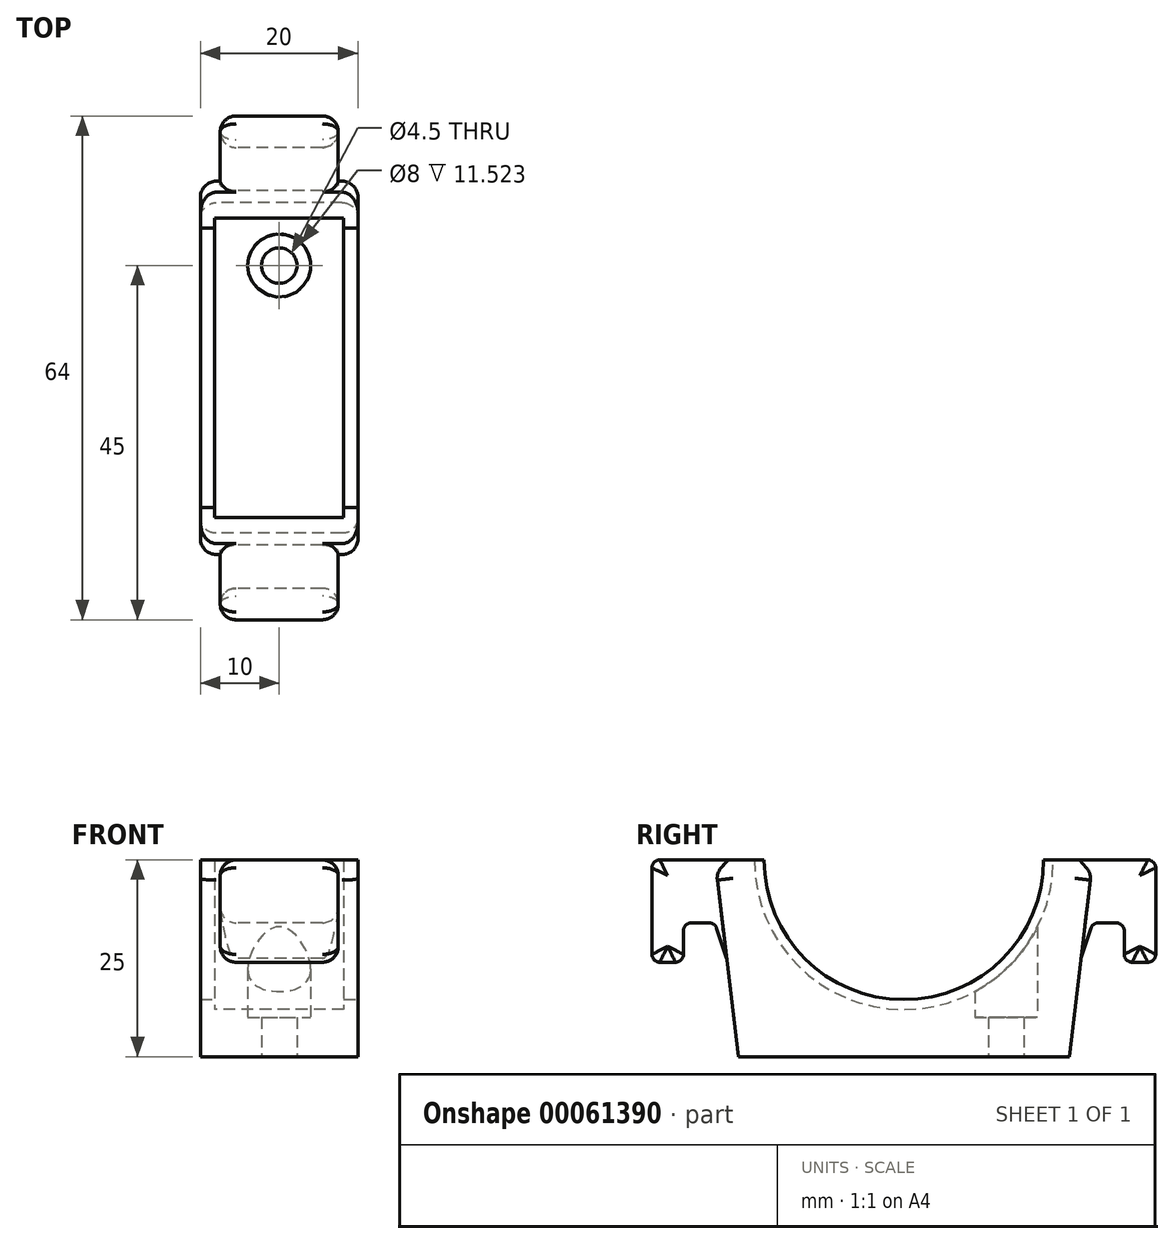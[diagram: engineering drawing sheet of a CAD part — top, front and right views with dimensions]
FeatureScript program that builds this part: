
annotation { "Feature Type Name" : "Feature", "Feature Type Description" : "" }
export const myFeature = defineFeature(function(context is Context, id is Id, definition is map)
    precondition{}
    {
        {
            var Q0;
            Q0=qCreatedBy(makeId("Right.planeOp"),FACE);
            var sketch = newSketch(context, id + "F0", { "sketchPlane" : qUnion([Q0])});
            skArc(sketch, "E0", {"start": v(-19, 0) * mm, "mid": v(0, -19) * mm, "end": v(19, 0) * mm});
            skLineSegment(sketch, "E1", {"start": v(19, 0) * mm, "end": v(24, 0) * mm});
            skLineSegment(sketch, "E2", {"start": v(24, 0) * mm, "end": v(21, -25) * mm});
            skLineSegment(sketch, "E3", {"start": v(21, -25) * mm, "end": v(-21, -25) * mm});
            skLineSegment(sketch, "E4", {"start": v(-21, -25) * mm, "end": v(-24, 0) * mm});
            skLineSegment(sketch, "E5", {"start": v(-24, 0) * mm, "end": v(-19, 0) * mm});
            skLineSegment(sketch, "E6", {"start": v(0, -19) * mm, "end": v(0, -25) * mm, "construction": true});
            skSolve(sketch);
        }
        {
            var Q0;
            Q0 = qSketchRegion(id + "F0", true);
            var Q1;
            Q1=sQuery(id+"F0.wireOp",EDGE,"E6");
            extrude(context, id + "F1", {"entities" : qUnion([Q0]), "surfaceEntities" : qUnion([Q1]), "endBound" : BoundingType.SYMMETRIC, "depth" : 20 * mm});
        }
        {
            var Q0;
            Q0=makeQuery(id+"F1.opExtrude","SWEPT_FACE",FACE,{"disambiguationData":[OSD([sQuery(id+"F0.wireOp",EDGE,"E3")])]});
            var sketch = newSketch(context, id + "F2", { "sketchPlane" : qUnion([Q0])});
            skCircle(sketch, "E7", {"center": v(0, -13) * mm, "radius": 2.25 * mm});
            skSolve(sketch);
        }
        {
            var Q0;
            Q0 = qSketchRegion(id + "F2", true);
            extrude(context, id + "F3", {"entities" : qUnion([Q0]), "operationType" : NewBodyOperationType.REMOVE, "oppositeDirection" : true, "depth" : 25 * mm});
        }
        {
            var Q0;
            Q0=makeQuery(id+"F1.opExtrude","SWEPT_FACE",FACE,{"disambiguationData":[OSD([sQuery(id+"F0.wireOp",EDGE,"E3")])]});
            cPlane(context, id + "F4", {"entities" : qUnion([Q0]), "cplaneType" : CPlaneType.OFFSET, "offset" : 5 * mm, "oppositeDirection" : true, "width" : 150 * mm, "height" : 150 * mm});
        }
        {
            var Q0;
            Q0=qCreatedBy(id+"F4.planeOp",FACE);
            var sketch = newSketch(context, id + "F5", { "sketchPlane" : qUnion([Q0])});
            skCircle(sketch, "E8", {"center": v(0, -13) * mm, "radius": 4 * mm});
            skSolve(sketch);
        }
        {
            var Q0;
            Q0 = qSketchRegion(id + "F5", true);
            extrude(context, id + "F6", {"entities" : qUnion([Q0]), "operationType" : NewBodyOperationType.REMOVE, "endBound" : BoundingType.THROUGH_ALL, "oppositeDirection" : true, "depth" : 25 * mm});
        }
        {
            var Q0;
            Q0=qCreatedBy(makeId("Right.planeOp"),FACE);
            var sketch = newSketch(context, id + "F7", { "sketchPlane" : qUnion([Q0])});
            skLineSegment(sketch, "E9", {"start": v(-24, 0) * mm, "end": v(-31, 0) * mm});
            skLineSegment(sketch, "E10", {"start": v(-32, -1) * mm, "end": v(-32, -12) * mm});
            skLineSegment(sketch, "E11", {"start": v(-31, -13) * mm, "end": v(-29, -13) * mm});
            skLineSegment(sketch, "E12", {"start": v(-28, -12) * mm, "end": v(-28, -9) * mm});
            skLineSegment(sketch, "E13", {"start": v(-27, -8) * mm, "end": v(-24.72, -8) * mm});
            skLineSegment(sketch, "E14", {"start": v(-23.77, -8.68) * mm, "end": v(-22.5, -12.5) * mm});
            skLineSegment(sketch, "E15", {"start": v(-22.5, -12.5) * mm, "end": v(-24, 0) * mm});
            skPoint(sketch, "E16.visualSharp", {"position": v(-32, 0) * mm});
            skArc(sketch, "E16.filletArc", {"start": v(-31, 0) * mm, "mid": v(-31.7, -0.3) * mm, "end": v(-32, -1) * mm});
            skPoint(sketch, "E17.visualSharp", {"position": v(-32, -13) * mm});
            skArc(sketch, "E17.filletArc", {"start": v(-32, -12) * mm, "mid": v(-31.7, -12.7) * mm, "end": v(-31, -13) * mm});
            skPoint(sketch, "E18.visualSharp", {"position": v(-28, -13) * mm});
            skArc(sketch, "E18.filletArc", {"start": v(-29, -13) * mm, "mid": v(-28.3, -12.7) * mm, "end": v(-28, -12) * mm});
            skPoint(sketch, "E19.visualSharp", {"position": v(-28, -8) * mm});
            skArc(sketch, "E19.filletArc", {"start": v(-27, -8) * mm, "mid": v(-27.7, -8.3) * mm, "end": v(-28, -9) * mm});
            skPoint(sketch, "E20.visualSharp", {"position": v(-24, -8) * mm});
            skArc(sketch, "E20.filletArc", {"start": v(-23.77, -8.68) * mm, "mid": v(-24.14, -8.19) * mm, "end": v(-24.72, -8) * mm});
            skLineSegment(sketch, "E21", {"start": v(0, 0) * mm, "end": v(0, -33.33) * mm, "construction": true});
            skLineSegment(sketch, "E22.MirrorCS", {"start": v(31, -13) * mm, "end": v(29, -13) * mm});
            skLineSegment(sketch, "E23.MirrorCS", {"start": v(28, -12) * mm, "end": v(28, -9) * mm});
            skLineSegment(sketch, "E24.MirrorCS", {"start": v(27, -8) * mm, "end": v(24.72, -8) * mm});
            skArc(sketch, "E25.MirrorCS", {"start": v(23.77, -8.68) * mm, "mid": v(24.14, -8.19) * mm, "end": v(24.72, -8) * mm});
            skLineSegment(sketch, "E26.MirrorCS", {"start": v(23.77, -8.68) * mm, "end": v(22.5, -12.5) * mm});
            skLineSegment(sketch, "E27.MirrorCS", {"start": v(22.5, -12.5) * mm, "end": v(24, 0) * mm});
            skPoint(sketch, "E28.MirrorP", {"position": v(28, -13) * mm});
            skArc(sketch, "E29.MirrorCS", {"start": v(31, 0) * mm, "mid": v(31.7, -0.3) * mm, "end": v(32, -1) * mm});
            skLineSegment(sketch, "E30.MirrorCS", {"start": v(32, -1) * mm, "end": v(32, -12) * mm});
            skLineSegment(sketch, "E31.MirrorCS", {"start": v(24, 0) * mm, "end": v(31, 0) * mm});
            skPoint(sketch, "E32.MirrorP", {"position": v(32, 0) * mm});
            skArc(sketch, "E33.MirrorCS", {"start": v(32, -12) * mm, "mid": v(31.7, -12.7) * mm, "end": v(31, -13) * mm});
            skArc(sketch, "E34.MirrorCS", {"start": v(29, -13) * mm, "mid": v(28.3, -12.7) * mm, "end": v(28, -12) * mm});
            skPoint(sketch, "E35.MirrorP", {"position": v(28, -8) * mm});
            skPoint(sketch, "E36.MirrorP", {"position": v(24, -8) * mm});
            skPoint(sketch, "E37.MirrorP", {"position": v(32, -13) * mm});
            skArc(sketch, "E38.MirrorCS", {"start": v(27, -8) * mm, "mid": v(27.7, -8.3) * mm, "end": v(28, -9) * mm});
            skSolve(sketch);
        }
        {
            var Q0;
            Q0 = qSketchRegion(id + "F7", true);
            extrude(context, id + "F8", {"entities" : qUnion([Q0]), "operationType" : NewBodyOperationType.ADD, "endBound" : BoundingType.SYMMETRIC, "depth" : 15 * mm});
        }
        {
            var Q0;
            Q0=makeQuery(id+"F8.opExtrude","CAP_EDGE",EDGE,{"disambiguationData":[OSD([sQuery(id+"F7.wireOp",EDGE,"E30.MirrorCS")])],"isStart":true});
            var Q1;
            Q1=makeQuery(id+"F8.opExtrude","CAP_EDGE",EDGE,{"disambiguationData":[OSD([sQuery(id+"F7.wireOp",EDGE,"E30.MirrorCS")])],"isStart":false});
            var Q2;
            Q2=makeQuery(id+"F8.opExtrude","CAP_EDGE",EDGE,{"disambiguationData":[OSD([sQuery(id+"F7.wireOp",EDGE,"E10")])],"isStart":true});
            var Q3;
            Q3=makeQuery(id+"F8.opExtrude","CAP_EDGE",EDGE,{"disambiguationData":[OSD([sQuery(id+"F7.wireOp",EDGE,"E10")])],"isStart":false});
            fillet(context, id + "F9", {"entities" : qUnion([Q0, Q1, Q2, Q3]), "radius" : 2 * mm, "tangentPropagation" : true, "allowEdgeOverflow" : false});
        }
        {
            var Q0;
            Q0=makeQuery(id+"F1.opExtrude","CAP_EDGE",EDGE,{"disambiguationData":[OSD([sQuery(id+"F0.wireOp",EDGE,"E2")])],"isStart":true});
            var Q1;
            Q1=makeQuery(id+"F1.opExtrude","CAP_EDGE",EDGE,{"disambiguationData":[OSD([sQuery(id+"F0.wireOp",EDGE,"E2")])],"isStart":false});
            var Q2;
            Q2=makeQuery(id+"F1.opExtrude","CAP_EDGE",EDGE,{"disambiguationData":[OSD([sQuery(id+"F0.wireOp",EDGE,"E4")])],"isStart":true});
            var Q3;
            Q3=makeQuery(id+"F1.opExtrude","CAP_EDGE",EDGE,{"disambiguationData":[OSD([sQuery(id+"F0.wireOp",EDGE,"E4")])],"isStart":false});
            fillet(context, id + "F10", {"entities" : qUnion([Q0, Q1, Q2, Q3]), "radius" : 2 * mm, "tangentPropagation" : true, "allowEdgeOverflow" : false});
        }
        {
            var Q0;
            Q0=makeQuery(id+"F8.boolean.opBoolean","MERGE",FACE,{"derivedFrom":[makeQuery(id+"F1.opExtrude","SWEPT_FACE",FACE,{"disambiguationData":[OSD([sQuery(id+"F0.wireOp",EDGE,"E1")])]}),makeQuery(id+"F8.opExtrude","SWEPT_FACE",FACE,{"disambiguationData":[OSD([sQuery(id+"F7.wireOp",EDGE,"E31.MirrorCS")])]})]});
            var sketch = newSketch(context, id + "F11", { "sketchPlane" : qUnion([Q0])});
            skLineSegment(sketch, "E39.bottom", {"start": v(-10, 19) * mm, "end": v(-8.2, 19) * mm});
            skLineSegment(sketch, "E39.top", {"start": v(-10, 17.75) * mm, "end": v(-8.2, 17.75) * mm});
            skLineSegment(sketch, "E39.left", {"start": v(-10, 19) * mm, "end": v(-10, 17.75) * mm});
            skLineSegment(sketch, "E39.right", {"start": v(-8.2, 19) * mm, "end": v(-8.2, 17.75) * mm});
            skLineSegment(sketch, "E40.bottom", {"start": v(10, 19) * mm, "end": v(8.2, 19) * mm});
            skLineSegment(sketch, "E40.top", {"start": v(10, 17.75) * mm, "end": v(8.2, 17.75) * mm});
            skLineSegment(sketch, "E40.left", {"start": v(10, 19) * mm, "end": v(10, 17.75) * mm});
            skLineSegment(sketch, "E40.right", {"start": v(8.2, 19) * mm, "end": v(8.2, 17.75) * mm});
            skLineSegment(sketch, "E41", {"start": v(0, 0) * mm, "end": v(25.5, 0) * mm, "construction": true});
            skSolve(sketch);
        }
        {
            var Q0;
            Q0=makeQuery(id+"F11.imprint","IMPRINT",FACE,{"disambiguationData":[TD([[makeQuery(id+"F11.imprint","IMPRINT",EDGE,{"derivedFrom":sQuery(id+"F11.wireOp",EDGE,"E39.bottom")}),1.0]])]});
            var Q1;
            Q1=makeQuery(id+"F11.imprint","IMPRINT",FACE,{"disambiguationData":[TD([[makeQuery(id+"F11.imprint","IMPRINT",EDGE,{"derivedFrom":sQuery(id+"F11.wireOp",EDGE,"E40.bottom")}),1.0]])]});
            var Q2;
            Q2=sQuery(id+"F11.wireOp",EDGE,"E39.bottom");
            var Q3;
            Q3=sQuery(id+"F11.wireOp",EDGE,"E39.top");
            var Q4;
            Q4=sQuery(id+"F11.wireOp",EDGE,"E39.left");
            var Q5;
            Q5=sQuery(id+"F11.wireOp",EDGE,"E39.right");
            var Q6;
            Q6=sQuery(id+"F11.wireOp",EDGE,"E40.top");
            var Q7;
            Q7=sQuery(id+"F11.wireOp",EDGE,"E40.left");
            var Q8;
            Q8=sQuery(id+"F11.wireOp",EDGE,"E40.right");
            var Q9;
            Q9=sQuery(id+"F11.wireOp",EDGE,"E40.bottom");
            var Q10;
            Q10=sQuery(id+"F11.wireOp",EDGE,"E41");
            revolve(context, id + "F12", {"operationType" : NewBodyOperationType.ADD, "entities" : qUnion([Q0, Q1]), "surfaceEntities" : qUnion([Q2, Q3, Q4, Q5, Q6, Q7, Q8, Q9]), "axis" : qUnion([Q10]), "revolveType" : RevolveType.ONE_DIRECTION, "oppositeDirection" : true, "angle" : 180 * degree});
        }
        {
            var Q0;
            {var subQ0=sQuery(id+"F0.wireOp",EDGE,"E5");var subQ1=sQuery(id+"F0.wireOp",EDGE,"E4");Q0=makeQuery(id+"F8.boolean.opBoolean","SPLIT",EDGE,{"disambiguationData":[TD([makeQuery(id+"F1.opExtrude","CAP_FACE",FACE,{"disambiguationData":[OSD([sQuery(id+"F0.wireOp",EDGE,"E0"),sQuery(id+"F0.wireOp",EDGE,"E1"),sQuery(id+"F0.wireOp",EDGE,"E2"),sQuery(id+"F0.wireOp",EDGE,"E3"),subQ1,subQ0])],"isStart":false})])],"derivedFrom":makeQuery(id+"F1.opExtrude","SWEPT_EDGE",EDGE,{"disambiguationData":[OSD([subQ1,subQ0])]})});}
            var Q1;
            {var subQ1=sQuery(id+"F0.wireOp",EDGE,"E5");var subQ2=sQuery(id+"F0.wireOp",EDGE,"E4");Q1=makeQuery(id+"F8.boolean.opBoolean","SPLIT",EDGE,{"disambiguationData":[TD([makeQuery(id+"F1.opExtrude","CAP_FACE",FACE,{"disambiguationData":[OSD([sQuery(id+"F0.wireOp",EDGE,"E0"),sQuery(id+"F0.wireOp",EDGE,"E1"),sQuery(id+"F0.wireOp",EDGE,"E2"),sQuery(id+"F0.wireOp",EDGE,"E3"),subQ2,subQ1])],"isStart":true})])],"derivedFrom":makeQuery(id+"F1.opExtrude","SWEPT_EDGE",EDGE,{"disambiguationData":[OSD([subQ2,subQ1])]})});}
            var Q2;
            {var subQ0=sQuery(id+"F0.wireOp",EDGE,"E2");var subQ2=sQuery(id+"F0.wireOp",EDGE,"E1");Q2=makeQuery(id+"F8.boolean.opBoolean","SPLIT",EDGE,{"disambiguationData":[TD([makeQuery(id+"F1.opExtrude","CAP_FACE",FACE,{"disambiguationData":[OSD([sQuery(id+"F0.wireOp",EDGE,"E0"),subQ2,subQ0,sQuery(id+"F0.wireOp",EDGE,"E3"),sQuery(id+"F0.wireOp",EDGE,"E4"),sQuery(id+"F0.wireOp",EDGE,"E5")])],"isStart":false})])],"derivedFrom":makeQuery(id+"F1.opExtrude","SWEPT_EDGE",EDGE,{"disambiguationData":[OSD([subQ2,subQ0])]})});}
            var Q3;
            {var subQ0=sQuery(id+"F0.wireOp",EDGE,"E2");var subQ2=sQuery(id+"F0.wireOp",EDGE,"E1");Q3=makeQuery(id+"F8.boolean.opBoolean","SPLIT",EDGE,{"disambiguationData":[TD([makeQuery(id+"F1.opExtrude","CAP_FACE",FACE,{"disambiguationData":[OSD([sQuery(id+"F0.wireOp",EDGE,"E0"),subQ2,subQ0,sQuery(id+"F0.wireOp",EDGE,"E3"),sQuery(id+"F0.wireOp",EDGE,"E4"),sQuery(id+"F0.wireOp",EDGE,"E5")])],"isStart":true})])],"derivedFrom":makeQuery(id+"F1.opExtrude","SWEPT_EDGE",EDGE,{"disambiguationData":[OSD([subQ2,subQ0])]})});}
            chamfer(context, id + "F13", {"entities" : qUnion([Q0, Q1, Q2, Q3]), "width" : 1.5 * mm});
        }
        {
            var Q0;
            {var subQ0=sQuery(id+"F0.wireOp",EDGE,"E4");var subQ1=makeQuery(id+"F1.opExtrude","SWEPT_FACE",FACE,{"disambiguationData":[OSD([subQ0])]});var subQ3=sQuery(id+"F0.wireOp",EDGE,"E5");Q0=makeQuery(id+"F13.opChamfer","BLEND_EDGE",EDGE,{"blendedFrom":[makeQuery(id+"F8.boolean.opBoolean","SPLIT",EDGE,{"disambiguationData":[TD([makeQuery(id+"F1.opExtrude","CAP_FACE",FACE,{"disambiguationData":[OSD([sQuery(id+"F0.wireOp",EDGE,"E0"),sQuery(id+"F0.wireOp",EDGE,"E1"),sQuery(id+"F0.wireOp",EDGE,"E2"),sQuery(id+"F0.wireOp",EDGE,"E3"),subQ0,subQ3])],"isStart":true})])],"derivedFrom":makeQuery(id+"F1.opExtrude","SWEPT_EDGE",EDGE,{"disambiguationData":[OSD([subQ0,subQ3])]})}),subQ1],"blendedInto":[subQ1]});}
            var Q1;
            {var subQ0=sQuery(id+"F0.wireOp",EDGE,"E4");var subQ1=makeQuery(id+"F1.opExtrude","SWEPT_FACE",FACE,{"disambiguationData":[OSD([subQ0])]});var subQ2=sQuery(id+"F0.wireOp",EDGE,"E5");Q1=makeQuery(id+"F13.opChamfer","BLEND_EDGE",EDGE,{"blendedFrom":[makeQuery(id+"F8.boolean.opBoolean","SPLIT",EDGE,{"disambiguationData":[TD([makeQuery(id+"F1.opExtrude","CAP_FACE",FACE,{"disambiguationData":[OSD([sQuery(id+"F0.wireOp",EDGE,"E0"),sQuery(id+"F0.wireOp",EDGE,"E1"),sQuery(id+"F0.wireOp",EDGE,"E2"),sQuery(id+"F0.wireOp",EDGE,"E3"),subQ0,subQ2])],"isStart":false})])],"derivedFrom":makeQuery(id+"F1.opExtrude","SWEPT_EDGE",EDGE,{"disambiguationData":[OSD([subQ0,subQ2])]})}),subQ1],"blendedInto":[subQ1]});}
            fillet(context, id + "F14", {"entities" : qUnion([Q0, Q1]), "radius" : 2 * mm, "tangentPropagation" : true, "allowEdgeOverflow" : false});
        }
        {
            var Q0;
            {var subQ0=sQuery(id+"F0.wireOp",EDGE,"E2");var subQ1=makeQuery(id+"F1.opExtrude","SWEPT_FACE",FACE,{"disambiguationData":[OSD([subQ0])]});var subQ3=sQuery(id+"F0.wireOp",EDGE,"E1");Q0=makeQuery(id+"F13.opChamfer","BLEND_EDGE",EDGE,{"blendedFrom":[makeQuery(id+"F8.boolean.opBoolean","SPLIT",EDGE,{"disambiguationData":[TD([makeQuery(id+"F1.opExtrude","CAP_FACE",FACE,{"disambiguationData":[OSD([sQuery(id+"F0.wireOp",EDGE,"E0"),subQ3,subQ0,sQuery(id+"F0.wireOp",EDGE,"E3"),sQuery(id+"F0.wireOp",EDGE,"E4"),sQuery(id+"F0.wireOp",EDGE,"E5")])],"isStart":false})])],"derivedFrom":makeQuery(id+"F1.opExtrude","SWEPT_EDGE",EDGE,{"disambiguationData":[OSD([subQ3,subQ0])]})}),subQ1],"blendedInto":[subQ1]});}
            var Q1;
            {var subQ0=sQuery(id+"F0.wireOp",EDGE,"E2");var subQ1=makeQuery(id+"F1.opExtrude","SWEPT_FACE",FACE,{"disambiguationData":[OSD([subQ0])]});var subQ3=sQuery(id+"F0.wireOp",EDGE,"E1");Q1=makeQuery(id+"F13.opChamfer","BLEND_EDGE",EDGE,{"blendedFrom":[makeQuery(id+"F8.boolean.opBoolean","SPLIT",EDGE,{"disambiguationData":[TD([makeQuery(id+"F1.opExtrude","CAP_FACE",FACE,{"disambiguationData":[OSD([sQuery(id+"F0.wireOp",EDGE,"E0"),subQ3,subQ0,sQuery(id+"F0.wireOp",EDGE,"E3"),sQuery(id+"F0.wireOp",EDGE,"E4"),sQuery(id+"F0.wireOp",EDGE,"E5")])],"isStart":true})])],"derivedFrom":makeQuery(id+"F1.opExtrude","SWEPT_EDGE",EDGE,{"disambiguationData":[OSD([subQ3,subQ0])]})}),subQ1],"blendedInto":[subQ1]});}
            fillet(context, id + "F15", {"entities" : qUnion([Q0, Q1]), "radius" : 2 * mm, "tangentPropagation" : true, "allowEdgeOverflow" : false});
        }
    });
